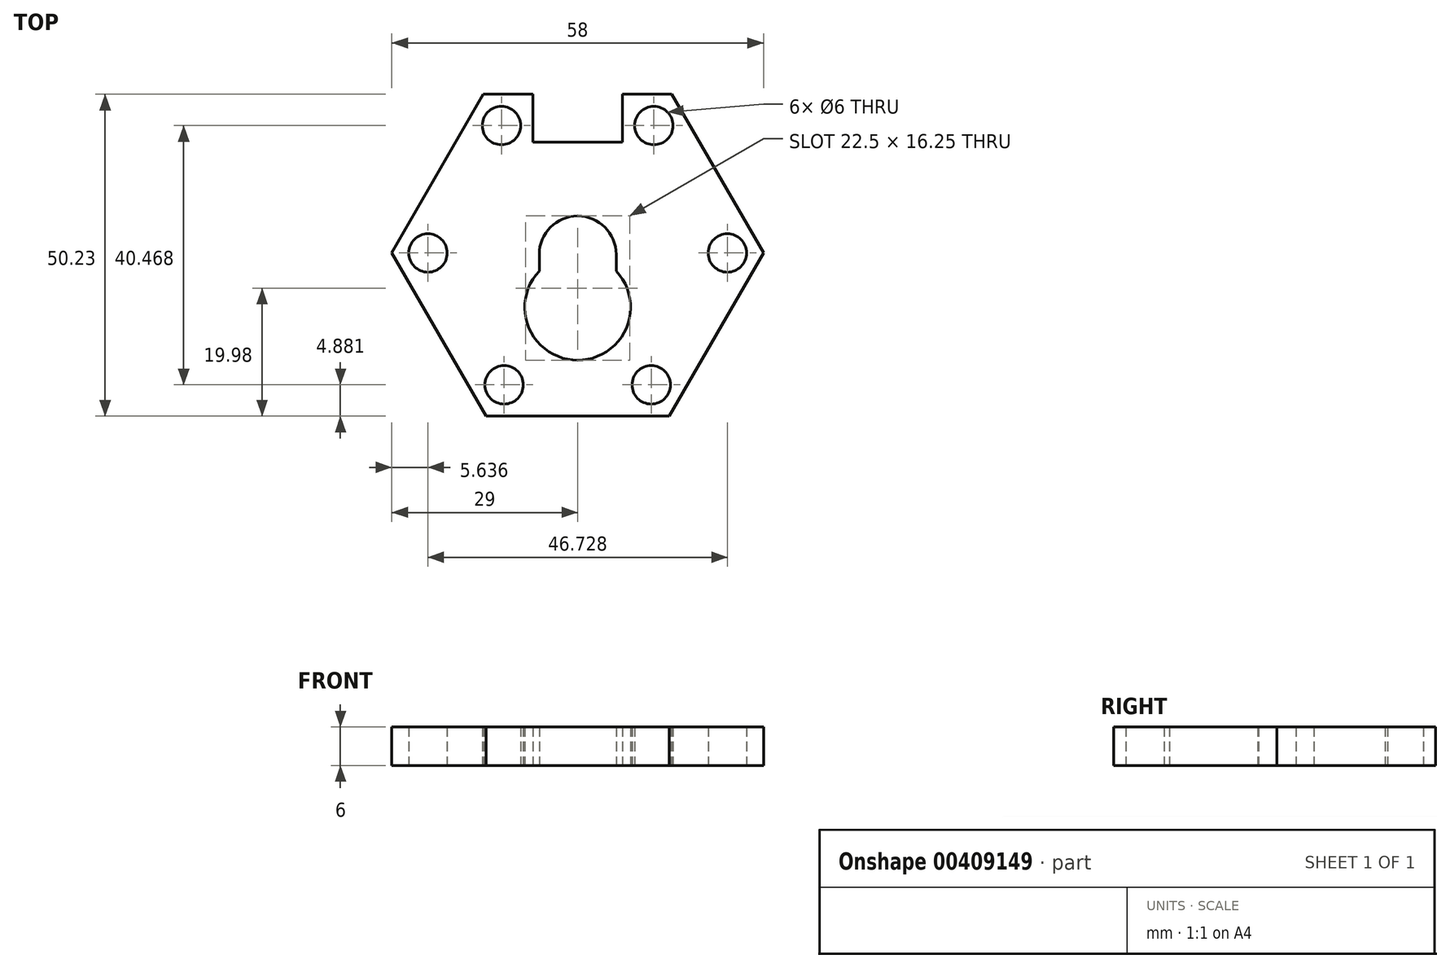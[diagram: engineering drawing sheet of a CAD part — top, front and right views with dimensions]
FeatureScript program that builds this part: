
annotation { "Feature Type Name" : "Feature", "Feature Type Description" : "" }
export const myFeature = defineFeature(function(context is Context, id is Id, definition is map)
    precondition{}
    {
        {
            var Q0;
            Q0=qCreatedBy(makeId("Top.planeOp"),FACE);
            var sketch = newSketch(context, id + "F0", { "sketchPlane" : qUnion([Q0])});
            skCircle(sketch, "E0", {"center": v(0, 0) * mm, "radius": 27 * mm, "construction": true});
            skLineSegment(sketch, "E1", {"start": v(-29, 27) * mm, "end": v(29, 27) * mm, "construction": true});
            skLineSegment(sketch, "E2", {"start": v(-37.88, 11.61) * mm, "end": v(-8.88, -38.61) * mm, "construction": true});
            skLineSegment(sketch, "E3", {"start": v(8.88, -38.61) * mm, "end": v(37.88, 11.61) * mm, "construction": true});
            skLineSegment(sketch, "E4", {"start": v(-23.38, -13.5) * mm, "end": v(0, 0) * mm, "construction": true});
            skLineSegment(sketch, "E5", {"start": v(0, 0) * mm, "end": v(23.38, -13.5) * mm, "construction": true});
            skLineSegment(sketch, "E6", {"start": v(0, 27) * mm, "end": v(0, 0) * mm, "construction": true});
            skCircle(sketch, "E7", {"center": v(0, 27) * mm, "radius": 2 * mm, "construction": true});
            skCircle(sketch, "E8", {"center": v(-23.38, -13.5) * mm, "radius": 2 * mm, "construction": true});
            skCircle(sketch, "E9", {"center": v(23.38, -13.5) * mm, "radius": 2 * mm, "construction": true});
            skLineSegment(sketch, "E10", {"start": v(-14.7, 25) * mm, "end": v(14.7, 25) * mm, "construction": true});
            skLineSegment(sketch, "E11", {"start": v(-29, 0.23) * mm, "end": v(-14.3, -25.23) * mm});
            skLineSegment(sketch, "E12", {"start": v(14.3, -25.23) * mm, "end": v(29, 0.23) * mm});
            skLineSegment(sketch, "E13", {"start": v(-14.7, 25) * mm, "end": v(-29, 0.23) * mm});
            skLineSegment(sketch, "E14", {"start": v(-14.3, -25.23) * mm, "end": v(14.3, -25.23) * mm});
            skLineSegment(sketch, "E15", {"start": v(29, 0.23) * mm, "end": v(14.7, 25) * mm});
            skLineSegment(sketch, "E16", {"start": v(-7, 25) * mm, "end": v(-7, 17.5) * mm});
            skLineSegment(sketch, "E17", {"start": v(-7, 17.5) * mm, "end": v(7, 17.5) * mm});
            skLineSegment(sketch, "E18", {"start": v(7, 17.5) * mm, "end": v(7, 25) * mm});
            skLineSegment(sketch, "E19", {"start": v(-14.7, 25) * mm, "end": v(-7, 25) * mm});
            skLineSegment(sketch, "E20", {"start": v(7, 25) * mm, "end": v(14.7, 25) * mm});
            skArc(sketch, "E21", {"start": v(-6, 0) * mm, "mid": v(0, 6) * mm, "end": v(6, 0) * mm});
            skLineSegment(sketch, "E22", {"start": v(-6, 0) * mm, "end": v(-6, -2.59) * mm});
            skLineSegment(sketch, "E23", {"start": v(6, 0) * mm, "end": v(6, -2.59) * mm});
            skArc(sketch, "E24", {"start": v(-6, -2.59) * mm, "mid": v(0, -16.5) * mm, "end": v(6, -2.59) * mm});
            skCircle(sketch, "E25", {"center": v(-11.88, 20.12) * mm, "radius": 3 * mm});
            skCircle(sketch, "E26", {"center": v(-11.88, 20.12) * mm, "radius": 4.88 * mm, "construction": true});
            skCircle(sketch, "E27.MirrorC", {"center": v(11.88, 20.12) * mm, "radius": 3 * mm});
            skCircle(sketch, "E28.1.0", {"center": v(-11.48, -20.35) * mm, "radius": 3 * mm});
            skCircle(sketch, "E28.1.1", {"center": v(-23.36, 0.23) * mm, "radius": 3 * mm});
            skCircle(sketch, "E28.2.0", {"center": v(23.36, 0.23) * mm, "radius": 3 * mm});
            skCircle(sketch, "E28.2.1", {"center": v(11.48, -20.35) * mm, "radius": 3 * mm});
            skLineSegment(sketch, "E29", {"start": v(-29, 27) * mm, "end": v(-29, 0.23) * mm, "construction": true});
            skSolve(sketch);
        }
        {
            var Q0;
            Q0=makeQuery(id+"F0.imprint","IMPRINT",FACE,{"disambiguationData":[TD([[makeQuery(id+"F0.imprint","IMPRINT",EDGE,{"derivedFrom":sQuery(id+"F0.wireOp",EDGE,"E11")}),1.0]])]});
            extrude(context, id + "F1", {"entities" : qUnion([Q0]), "depth" : 6 * mm, "offsetDistance" : 25 * mm});
        }
    });
